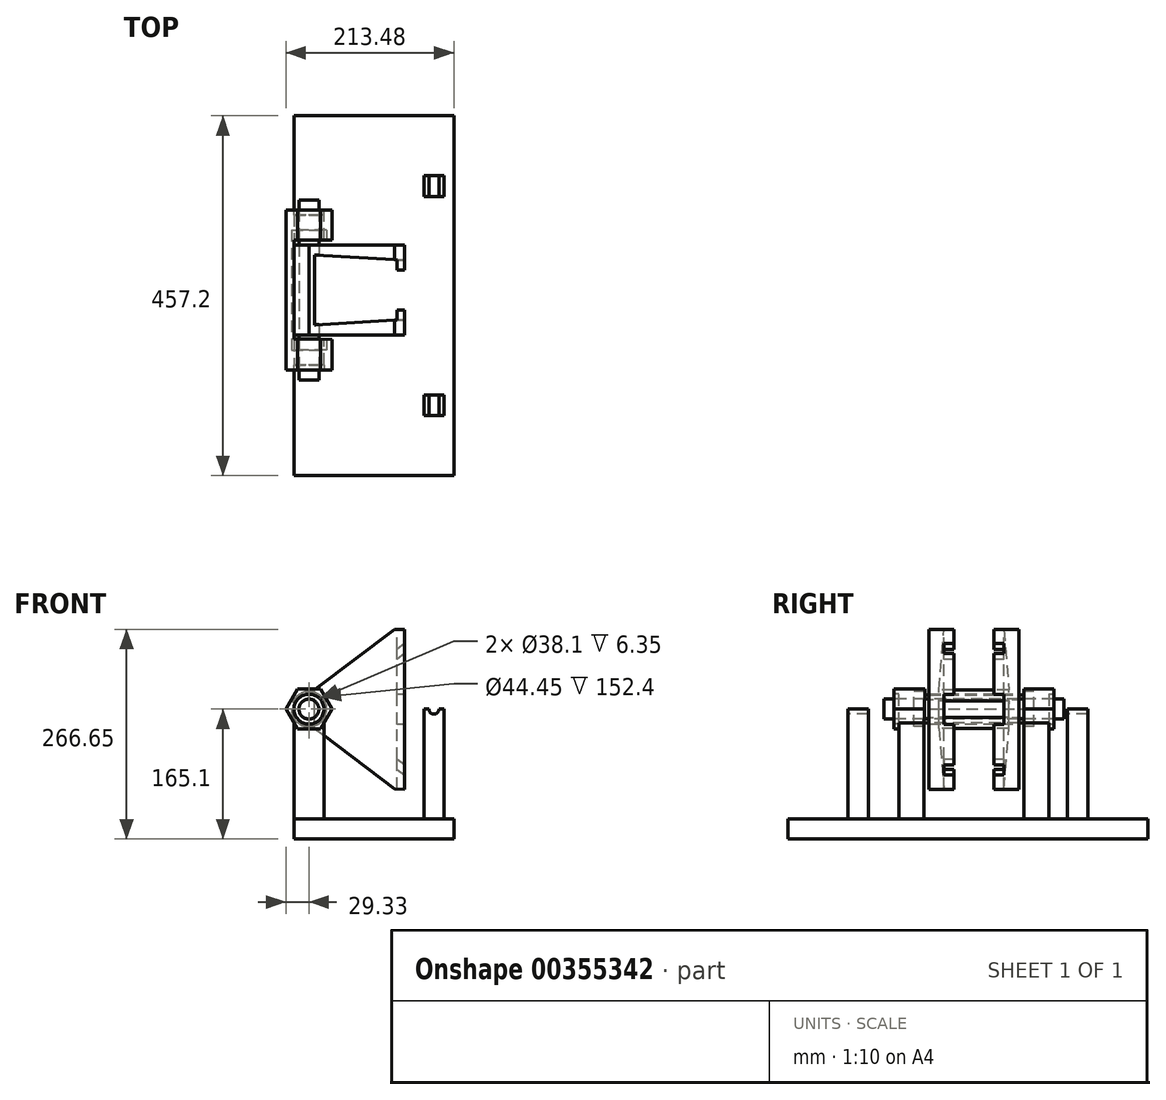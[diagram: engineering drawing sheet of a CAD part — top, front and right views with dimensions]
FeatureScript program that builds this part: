
annotation { "Feature Type Name" : "Feature", "Feature Type Description" : "" }
export const myFeature = defineFeature(function(context is Context, id is Id, definition is map)
    precondition{}
    {
        {
            var Q0;
            Q0=qCreatedBy(makeId("Right.planeOp"),FACE);
            var sketch = newSketch(context, id + "F0", { "sketchPlane" : qUnion([Q0])});
            skLineSegment(sketch, "E0.bottom", {"start": v(0, 0) * mm, "end": v(457.2, 0) * mm});
            skLineSegment(sketch, "E0.top", {"start": v(0, 25.4) * mm, "end": v(457.2, 25.4) * mm});
            skLineSegment(sketch, "E0.left", {"start": v(0, 0) * mm, "end": v(0, 25.4) * mm});
            skLineSegment(sketch, "E0.right", {"start": v(457.2, 0) * mm, "end": v(457.2, 25.4) * mm});
            skSolve(sketch);
        }
        {
            var Q0;
            Q0 = qSketchRegion(id + "F0", true);
            extrude(context, id + "F1", {"entities" : qUnion([Q0]), "oppositeDirection" : true, "depth" : 203.2 * mm});
        }
        {
            var Q0;
            Q0=makeQuery(id+"F1.opExtrude","CAP_FACE",FACE,{"disambiguationData":[OSD([sQuery(id+"F0.wireOp",EDGE,"E0.bottom"),sQuery(id+"F0.wireOp",EDGE,"E0.top"),sQuery(id+"F0.wireOp",EDGE,"E0.left"),sQuery(id+"F0.wireOp",EDGE,"E0.right")])],"isStart":true});
            var sketch = newSketch(context, id + "F2", { "sketchPlane" : qUnion([Q0])});
            skLineSegment(sketch, "E1.bottom", {"start": v(76.2, 25.4) * mm, "end": v(102.38, 25.4) * mm});
            skLineSegment(sketch, "E1.top", {"start": v(76.2, 165.1) * mm, "end": v(102.38, 165.1) * mm});
            skLineSegment(sketch, "E1.left", {"start": v(76.2, 25.4) * mm, "end": v(76.2, 165.1) * mm});
            skLineSegment(sketch, "E1.right", {"start": v(102.38, 25.4) * mm, "end": v(102.38, 165.1) * mm});
            skLineSegment(sketch, "E2", {"start": v(228.6, 68.14) * mm, "end": v(228.6, -33.61) * mm});
            skPoint(sketch, "E2.startSnap0", {"position": v(228.6, 25.4) * mm});
            skLineSegment(sketch, "E3.MirrorCS", {"start": v(381, 25.4) * mm, "end": v(381, 165.1) * mm});
            skLineSegment(sketch, "E4.MirrorCS", {"start": v(381, 25.4) * mm, "end": v(354.82, 25.4) * mm});
            skLineSegment(sketch, "E5.MirrorCS", {"start": v(354.82, 25.4) * mm, "end": v(354.82, 165.1) * mm});
            skLineSegment(sketch, "E6.MirrorCS", {"start": v(381, 165.1) * mm, "end": v(354.82, 165.1) * mm});
            skSolve(sketch);
        }
        {
            var Q0;
            Q0 = qSketchRegion(id + "F2", true);
            extrude(context, id + "F3", {"entities" : qUnion([Q0]), "oppositeDirection" : true, "depth" : 38.1 * mm});
        }
        {
            var Q0;
            Q0=makeQuery(id+"F3.opExtrude","SWEPT_FACE",FACE,{"disambiguationData":[OSD([sQuery(id+"F2.wireOp",EDGE,"E1.left")])]});
            var sketch = newSketch(context, id + "F4", { "sketchPlane" : qUnion([Q0])});
            skLineSegment(sketch, "E7.bottom", {"start": v(0, 25.4) * mm, "end": v(-12.7, 25.4) * mm});
            skLineSegment(sketch, "E7.top", {"start": v(0, 165.1) * mm, "end": v(-12.7, 165.1) * mm});
            skLineSegment(sketch, "E7.left", {"start": v(0, 25.4) * mm, "end": v(0, 165.1) * mm});
            skLineSegment(sketch, "E7.right", {"start": v(-12.7, 25.4) * mm, "end": v(-12.7, 165.1) * mm});
            skSolve(sketch);
        }
        {
            var Q0;
            Q0 = qSketchRegion(id + "F4", true);
            extrude(context, id + "F5", {"entities" : qUnion([Q0]), "operationType" : NewBodyOperationType.REMOVE, "endBound" : BoundingType.THROUGH_ALL, "oppositeDirection" : true, "depth" : 25.4 * mm});
        }
        {
            var Q0;
            Q0=makeQuery(id+"F1.opExtrude","CAP_FACE",FACE,{"disambiguationData":[OSD([sQuery(id+"F0.wireOp",EDGE,"E0.bottom"),sQuery(id+"F0.wireOp",EDGE,"E0.top"),sQuery(id+"F0.wireOp",EDGE,"E0.left"),sQuery(id+"F0.wireOp",EDGE,"E0.right")])],"isStart":false});
            var sketch = newSketch(context, id + "F6", { "sketchPlane" : qUnion([Q0])});
            skLineSegment(sketch, "E8.bottom", {"start": v(-331.33, 25.4) * mm, "end": v(-299.58, 25.4) * mm});
            skLineSegment(sketch, "E8.top", {"start": v(-331.33, 177.8) * mm, "end": v(-299.58, 177.8) * mm});
            skLineSegment(sketch, "E8.left", {"start": v(-331.33, 25.4) * mm, "end": v(-331.33, 177.8) * mm});
            skLineSegment(sketch, "E8.right", {"start": v(-299.58, 25.4) * mm, "end": v(-299.58, 177.8) * mm});
            skLineSegment(sketch, "E9.bottom", {"start": v(-172.58, 25.4) * mm, "end": v(-140.83, 25.4) * mm});
            skLineSegment(sketch, "E9.top", {"start": v(-172.58, 177.8) * mm, "end": v(-140.83, 177.8) * mm});
            skLineSegment(sketch, "E9.left", {"start": v(-172.58, 25.4) * mm, "end": v(-172.58, 177.8) * mm});
            skLineSegment(sketch, "E9.right", {"start": v(-140.83, 25.4) * mm, "end": v(-140.83, 177.8) * mm});
            skSolve(sketch);
        }
        {
            var Q0;
            Q0 = qSketchRegion(id + "F6", true);
            extrude(context, id + "F7", {"entities" : qUnion([Q0]), "operationType" : NewBodyOperationType.ADD, "oppositeDirection" : true, "depth" : 38.1 * mm});
        }
        {
            var Q0;
            Q0=makeQuery(id+"F7.opExtrude","SWEPT_FACE",FACE,{"disambiguationData":[OSD([sQuery(id+"F6.wireOp",EDGE,"E8.left")])]});
            var sketch = newSketch(context, id + "F8", { "sketchPlane" : qUnion([Q0])});
            skPoint(sketch, "E10", {"position": v(184.15, 165.1) * mm});
            skPoint(sketch, "E10.positionSnap0", {"position": v(184.15, 177.8) * mm});
            skCircle(sketch, "E11.cCircle", {"center": v(184.15, 165.1) * mm, "radius": 25.4 * mm, "construction": true});
            skLineSegment(sketch, "E11.0", {"start": v(169.49, 190.5) * mm, "end": v(198.81, 190.5) * mm});
            skLineSegment(sketch, "E11.1", {"start": v(198.81, 190.5) * mm, "end": v(213.48, 165.1) * mm});
            skLineSegment(sketch, "E11.2", {"start": v(213.48, 165.1) * mm, "end": v(198.81, 139.7) * mm});
            skLineSegment(sketch, "E11.3", {"start": v(198.81, 139.7) * mm, "end": v(169.49, 139.7) * mm});
            skLineSegment(sketch, "E11.4", {"start": v(169.49, 139.7) * mm, "end": v(154.82, 165.1) * mm});
            skLineSegment(sketch, "E11.5", {"start": v(154.82, 165.1) * mm, "end": v(169.49, 190.5) * mm});
            skPoint(sketch, "E11.0.midPoint", {"position": v(184.15, 190.5) * mm});
            skSolve(sketch);
        }
        {
            var Q0;
            Q0 = qSketchRegion(id + "F8", true);
            extrude(context, id + "F9", {"entities" : qUnion([Q0]), "operationType" : NewBodyOperationType.ADD, "oppositeDirection" : true, "depth" : 196.85 * mm, "hasSecondDirection" : true, "secondDirectionOppositeDirection" : false, "secondDirectionDepth" : 6.35 * mm});
        }
        {
            var Q0;
            Q0=makeQuery(id+"F7.boolean.opBoolean","MERGE",FACE,{"derivedFrom":[makeQuery(id+"F1.opExtrude","CAP_FACE",FACE,{"disambiguationData":[OSD([sQuery(id+"F0.wireOp",EDGE,"E0.bottom"),sQuery(id+"F0.wireOp",EDGE,"E0.top"),sQuery(id+"F0.wireOp",EDGE,"E0.left"),sQuery(id+"F0.wireOp",EDGE,"E0.right")])],"isStart":false}),makeQuery(id+"F7.opExtrude","CAP_FACE",FACE,{"disambiguationData":[OSD([sQuery(id+"F6.wireOp",EDGE,"E8.bottom"),sQuery(id+"F6.wireOp",EDGE,"E8.top"),sQuery(id+"F6.wireOp",EDGE,"E8.left"),sQuery(id+"F6.wireOp",EDGE,"E8.right")])],"isStart":true}),makeQuery(id+"F7.opExtrude","CAP_FACE",FACE,{"disambiguationData":[OSD([sQuery(id+"F6.wireOp",EDGE,"E9.bottom"),sQuery(id+"F6.wireOp",EDGE,"E9.top"),sQuery(id+"F6.wireOp",EDGE,"E9.left"),sQuery(id+"F6.wireOp",EDGE,"E9.right")])],"isStart":true})]});
            var sketch = newSketch(context, id + "F10", { "sketchPlane" : qUnion([Q0])});
            skLineSegment(sketch, "E12", {"start": v(-299.58, 139.7) * mm, "end": v(-299.58, 190.5) * mm});
            skLineSegment(sketch, "E13", {"start": v(-299.58, 190.5) * mm, "end": v(-173.69, 190.5) * mm});
            skLineSegment(sketch, "E14", {"start": v(-173.69, 190.5) * mm, "end": v(-172.58, 139.7) * mm});
            skLineSegment(sketch, "E15", {"start": v(-172.58, 139.7) * mm, "end": v(-299.58, 139.7) * mm});
            skSolve(sketch);
        }
        {
            var Q0;
            Q0 = qSketchRegion(id + "F10", true);
            extrude(context, id + "F11", {"entities" : qUnion([Q0]), "operationType" : NewBodyOperationType.REMOVE, "oppositeDirection" : true, "depth" : 50.8 * mm});
        }
        {
            var Q0;
            Q0=makeQuery(id+"F11.boolean.opBoolean","MERGE",FACE,{"derivedFrom":[makeQuery(id+"F7.opExtrude","SWEPT_FACE",FACE,{"disambiguationData":[OSD([sQuery(id+"F6.wireOp",EDGE,"E8.right")])]}),makeQuery(id+"F11.opExtrude","SWEPT_FACE",FACE,{"disambiguationData":[OSD([sQuery(id+"F10.wireOp",EDGE,"E12")])]})]});
            var sketch = newSketch(context, id + "F12", { "sketchPlane" : qUnion([Q0])});
            skPoint(sketch, "E16", {"position": v(-184.15, 165.1) * mm});
            skPoint(sketch, "E16.positionSnap0", {"position": v(-184.15, 190.5) * mm});
            skCircle(sketch, "E17", {"center": v(-184.15, 165.1) * mm, "radius": 22.23 * mm});
            skSolve(sketch);
        }
        {
            var Q0;
            Q0 = qSketchRegion(id + "F12", true);
            extrude(context, id + "F13", {"entities" : qUnion([Q0]), "operationType" : NewBodyOperationType.REMOVE, "oppositeDirection" : true, "depth" : 12.7 * mm, "hasSecondDirection" : true, "secondDirectionOppositeDirection" : false, "secondDirectionDepth" : 139.7 * mm});
        }
        {
            var Q0;
            Q0=makeQuery(id+"F9.opExtrude","CAP_FACE",FACE,{"disambiguationData":[OSD([sQuery(id+"F8.wireOp",EDGE,"E11.0"),sQuery(id+"F8.wireOp",EDGE,"E11.1"),sQuery(id+"F8.wireOp",EDGE,"E11.2"),sQuery(id+"F8.wireOp",EDGE,"E11.3"),sQuery(id+"F8.wireOp",EDGE,"E11.4"),sQuery(id+"F8.wireOp",EDGE,"E11.5")])],"isStart":false});
            var sketch = newSketch(context, id + "F14", { "sketchPlane" : qUnion([Q0])});
            skPoint(sketch, "E18", {"position": v(-184.15, 165.1) * mm});
            skPoint(sketch, "E18.positionSnap0", {"position": v(-184.15, 190.5) * mm});
            skCircle(sketch, "E19", {"center": v(-184.15, 165.1) * mm, "radius": 19.05 * mm});
            skSolve(sketch);
        }
        {
            var Q0;
            Q0 = qSketchRegion(id + "F14", true);
            extrude(context, id + "F15", {"entities" : qUnion([Q0]), "operationType" : NewBodyOperationType.REMOVE, "oppositeDirection" : true, "depth" : 6.35 * mm});
        }
        {
            var Q0;
            Q0=makeQuery(id+"F9.opExtrude","CAP_FACE",FACE,{"disambiguationData":[OSD([sQuery(id+"F8.wireOp",EDGE,"E11.0"),sQuery(id+"F8.wireOp",EDGE,"E11.1"),sQuery(id+"F8.wireOp",EDGE,"E11.2"),sQuery(id+"F8.wireOp",EDGE,"E11.3"),sQuery(id+"F8.wireOp",EDGE,"E11.4"),sQuery(id+"F8.wireOp",EDGE,"E11.5")])],"isStart":true});
            var sketch = newSketch(context, id + "F16", { "sketchPlane" : qUnion([Q0])});
            skPoint(sketch, "E20", {"position": v(184.15, 165.1) * mm});
            skPoint(sketch, "E20.positionSnap0", {"position": v(184.15, 190.5) * mm});
            skCircle(sketch, "E21", {"center": v(184.15, 165.1) * mm, "radius": 19.05 * mm});
            skSolve(sketch);
        }
        {
            var Q0;
            Q0 = qSketchRegion(id + "F16", true);
            extrude(context, id + "F17", {"entities" : qUnion([Q0]), "operationType" : NewBodyOperationType.REMOVE, "oppositeDirection" : true, "depth" : 6.35 * mm});
        }
        {
            var Q0;
            Q0=makeQuery(id+"F11.boolean.opBoolean","MERGE",FACE,{"derivedFrom":[makeQuery(id+"F7.opExtrude","SWEPT_FACE",FACE,{"disambiguationData":[OSD([sQuery(id+"F6.wireOp",EDGE,"E8.right")])]}),makeQuery(id+"F11.opExtrude","SWEPT_FACE",FACE,{"disambiguationData":[OSD([sQuery(id+"F10.wireOp",EDGE,"E12")])]})]});
            cPlane(context, id + "F18", {"entities" : qUnion([Q0]), "cplaneType" : CPlaneType.OFFSET, "offset" : 6.35 * mm, "width" : 152.4 * mm, "height" : 152.4 * mm});
        }
        {
            var Q0;
            Q0=makeQuery(id+"F13.boolean.opBoolean","COPY",FACE,{"derivedFrom":makeQuery(id+"F13.opExtrude","CAP_FACE",FACE,{"disambiguationData":[OSD([sQuery(id+"F12.wireOp",EDGE,"E17")])],"isStart":true})});
            var sketch = newSketch(context, id + "F19", { "sketchPlane" : qUnion([Q0])});
            skCircle(sketch, "E22", {"center": v(184.15, 165.1) * mm, "radius": 12.7 * mm});
            skSolve(sketch);
        }
        {
            var Q0;
            Q0 = qSketchRegion(id + "F19", true);
            extrude(context, id + "F20", {"entities" : qUnion([Q0]), "depth" : 190.5 * mm, "hasSecondDirection" : true, "secondDirectionOppositeDirection" : true, "secondDirectionDepth" : 38.1 * mm});
        }
        {
            var Q0;
            Q0=qCreatedBy(id+"F18.planeOp",FACE);
            var sketch = newSketch(context, id + "F21", { "sketchPlane" : qUnion([Q0])});
            skCircle(sketch, "E23", {"center": v(-184.15, 165.1) * mm, "radius": 19.05 * mm});
            skLineSegment(sketch, "E24", {"start": v(-184.15, 184.15) * mm, "end": v(-75.32, 266.65) * mm});
            skLineSegment(sketch, "E25", {"start": v(-184.15, 184.15) * mm, "end": v(-184.15, 165.1) * mm});
            skPoint(sketch, "E26", {"position": v(-62.62, 266.65) * mm});
            skPoint(sketch, "E27", {"position": v(-62.62, 165.05) * mm});
            skLineSegment(sketch, "E28", {"start": v(-75.32, 266.65) * mm, "end": v(-62.62, 266.65) * mm});
            skLineSegment(sketch, "E29", {"start": v(-62.62, 165.05) * mm, "end": v(-62.62, 266.65) * mm});
            skLineSegment(sketch, "E30", {"start": v(-62.62, 165.05) * mm, "end": v(-184.15, 165.1) * mm});
            skLineSegment(sketch, "E31.MirrorCS", {"start": v(-184.17, 146.05) * mm, "end": v(-184.15, 165.1) * mm});
            skLineSegment(sketch, "E32.MirrorCS", {"start": v(-184.17, 146.05) * mm, "end": v(-75.4, 63.46) * mm});
            skLineSegment(sketch, "E33.MirrorCS", {"start": v(-62.62, 165.05) * mm, "end": v(-62.7, 63.45) * mm});
            skLineSegment(sketch, "E34.MirrorCS", {"start": v(-75.4, 63.46) * mm, "end": v(-62.7, 63.45) * mm});
            skSolve(sketch);
        }
        {
            var Q0;
            Q0 = qSketchRegion(id + "F21", true);
            extrude(context, id + "F22", {"entities" : qUnion([Q0]), "depth" : 114.3 * mm});
        }
        {
            var Q0;
            Q0=makeQuery(id+"F22.opExtrude","SWEPT_FACE",FACE,{"disambiguationData":[OSD([sQuery(id+"F21.wireOp",EDGE,"E28")])]});
            var sketch = newSketch(context, id + "F23", { "sketchPlane" : qUnion([Q0])});
            skPoint(sketch, "E35", {"position": v(-72.14, 274.18) * mm});
            skPoint(sketch, "E36", {"position": v(-176.84, 280.53) * mm});
            skPoint(sketch, "E37", {"position": v(-72.14, 197.98) * mm});
            skPoint(sketch, "E38", {"position": v(-176.84, 191.63) * mm});
            skLineSegment(sketch, "E39", {"start": v(-72.14, 274.18) * mm, "end": v(-176.84, 280.53) * mm});
            skLineSegment(sketch, "E40", {"start": v(-176.84, 280.53) * mm, "end": v(-176.84, 191.63) * mm});
            skLineSegment(sketch, "E41", {"start": v(-176.84, 191.63) * mm, "end": v(-72.14, 197.98) * mm});
            skLineSegment(sketch, "E42", {"start": v(-72.14, 274.18) * mm, "end": v(-72.14, 197.98) * mm});
            skSolve(sketch);
        }
        {
            var Q0;
            Q0 = qSketchRegion(id + "F23", true);
            extrude(context, id + "F24", {"entities" : qUnion([Q0]), "operationType" : NewBodyOperationType.REMOVE, "oppositeDirection" : true, "depth" : 209.55 * mm});
        }
        {
            var Q0;
            Q0=makeQuery(id+"F22.opExtrude","SWEPT_FACE",FACE,{"disambiguationData":[OSD([sQuery(id+"F21.wireOp",EDGE,"E28")])]});
            var sketch = newSketch(context, id + "F25", { "sketchPlane" : qUnion([Q0])});
            skPoint(sketch, "E43.positionSnap0", {"position": v(-68.97, 293.23) * mm});
            skPoint(sketch, "E44.positionSnap0", {"position": v(-68.97, 178.93) * mm});
            skLineSegment(sketch, "E45", {"start": v(-72.14, 261.48) * mm, "end": v(-62.62, 261.48) * mm});
            skLineSegment(sketch, "E46", {"start": v(-62.62, 261.48) * mm, "end": v(-62.62, 210.68) * mm});
            skLineSegment(sketch, "E47", {"start": v(-62.62, 210.68) * mm, "end": v(-72.14, 210.68) * mm});
            skLineSegment(sketch, "E48", {"start": v(-72.14, 210.68) * mm, "end": v(-72.14, 261.48) * mm});
            skSolve(sketch);
        }
        {
            var Q0;
            Q0 = qSketchRegion(id + "F25", true);
            extrude(context, id + "F26", {"entities" : qUnion([Q0]), "operationType" : NewBodyOperationType.REMOVE, "oppositeDirection" : true, "depth" : 209.55 * mm});
        }
        {
            var Q0;
            Q0=makeQuery(id+"F26.boolean.opBoolean","COPY",FACE,{"derivedFrom":makeQuery(id+"F26.opExtrude","SWEPT_FACE",FACE,{"disambiguationData":[OSD([sQuery(id+"F25.wireOp",EDGE,"E45")])]})});
            var sketch = newSketch(context, id + "F27", { "sketchPlane" : qUnion([Q0])});
            skPoint(sketch, "E49", {"position": v(-62.62, 184.1) * mm});
            skPoint(sketch, "E50", {"position": v(-72.14, 184.1) * mm});
            skPoint(sketch, "E51", {"position": v(-62.62, 235.78) * mm});
            skPoint(sketch, "E52", {"position": v(-72.14, 228.55) * mm});
            skPoint(sketch, "E53", {"position": v(-62.64, 146) * mm});
            skPoint(sketch, "E54", {"position": v(-72.14, 146) * mm});
            skPoint(sketch, "E55", {"position": v(-62.68, 94.36) * mm});
            skPoint(sketch, "E56", {"position": v(-72.14, 101.55) * mm});
            skLineSegment(sketch, "E57", {"start": v(-72.14, 228.55) * mm, "end": v(-62.62, 235.78) * mm});
            skLineSegment(sketch, "E58", {"start": v(-72.14, 101.55) * mm, "end": v(-62.68, 94.36) * mm});
            skPoint(sketch, "E59", {"position": v(-62.7, 81.66) * mm});
            skPoint(sketch, "E60", {"position": v(-72.14, 88.85) * mm});
            skPoint(sketch, "E61", {"position": v(-72.14, 241.25) * mm});
            skPoint(sketch, "E62", {"position": v(-62.62, 248.48) * mm});
            skLineSegment(sketch, "E63", {"start": v(-72.14, 184.1) * mm, "end": v(-62.62, 184.1) * mm});
            skLineSegment(sketch, "E64", {"start": v(-72.14, 146) * mm, "end": v(-62.64, 146) * mm});
            skLineSegment(sketch, "E65", {"start": v(-62.62, 248.48) * mm, "end": v(-62.62, 235.78) * mm});
            skLineSegment(sketch, "E66", {"start": v(-72.14, 241.25) * mm, "end": v(-62.62, 248.48) * mm});
            skLineSegment(sketch, "E67", {"start": v(-72.14, 241.25) * mm, "end": v(-72.14, 228.55) * mm});
            skLineSegment(sketch, "E68", {"start": v(-72.14, 88.85) * mm, "end": v(-72.14, 101.55) * mm});
            skLineSegment(sketch, "E69", {"start": v(-62.7, 81.66) * mm, "end": v(-62.68, 94.36) * mm});
            skLineSegment(sketch, "E70", {"start": v(-62.7, 81.66) * mm, "end": v(-72.14, 88.85) * mm});
            skLineSegment(sketch, "E71", {"start": v(-62.64, 146) * mm, "end": v(-62.62, 184.1) * mm});
            skLineSegment(sketch, "E72", {"start": v(-72.14, 184.1) * mm, "end": v(-72.14, 146) * mm});
            skPoint(sketch, "E73", {"position": v(-62.62, 165.05) * mm});
            skSolve(sketch);
        }
        {
            var Q0;
            Q0 = qSketchRegion(id + "F27", true);
            extrude(context, id + "F28", {"entities" : qUnion([Q0]), "operationType" : NewBodyOperationType.REMOVE, "oppositeDirection" : true, "depth" : 12.7 * mm, "hasSecondDirection" : true, "secondDirectionOppositeDirection" : false, "secondDirectionDepth" : 63.5 * mm});
        }
        {
            var Q0;
            Q0=makeQuery(id+"F3.opExtrude","SWEPT_FACE",FACE,{"disambiguationData":[OSD([sQuery(id+"F2.wireOp",EDGE,"E1.left")])]});
            var sketch = newSketch(context, id + "F29", { "sketchPlane" : qUnion([Q0])});
            skCircle(sketch, "E74", {"center": v(-25.4, 165.1) * mm, "radius": 6.35 * mm});
            skSolve(sketch);
        }
        {
            var Q0;
            Q0 = qSketchRegion(id + "F29", true);
            extrude(context, id + "F30", {"entities" : qUnion([Q0]), "operationType" : NewBodyOperationType.REMOVE, "oppositeDirection" : true, "depth" : 406.4 * mm});
        }
    });
